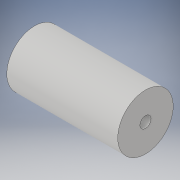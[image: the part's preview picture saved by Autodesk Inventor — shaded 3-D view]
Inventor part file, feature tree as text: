
AUTODESK INVENTOR PART (.ipt)
format: ipt  version: 2019 (Build 230136000, 136)  size: 103,424 bytes
history: native  units: mm
features: extrude x3, sketch x3, other x1
ambient origin geometry x8: Origin, YZ Plane, XZ Plane, XY Plane, X Axis, Y Axis, Z Axis, Center Point
bodies: Body1 (feature_tree)
feature tree (7):
  other  "Твердое тело1"
  extrude  "Выдавливание1"  Depth=10.0mm
  extrude  "Выдавливание2"  Depth=20.0mm TaperAngle=0.0deg
  extrude  "Выдавливание3"  Depth=2.15mm
  sketch  "Эскиз1"
  sketch  "Эскиз2"
  sketch  "Эскиз4"
